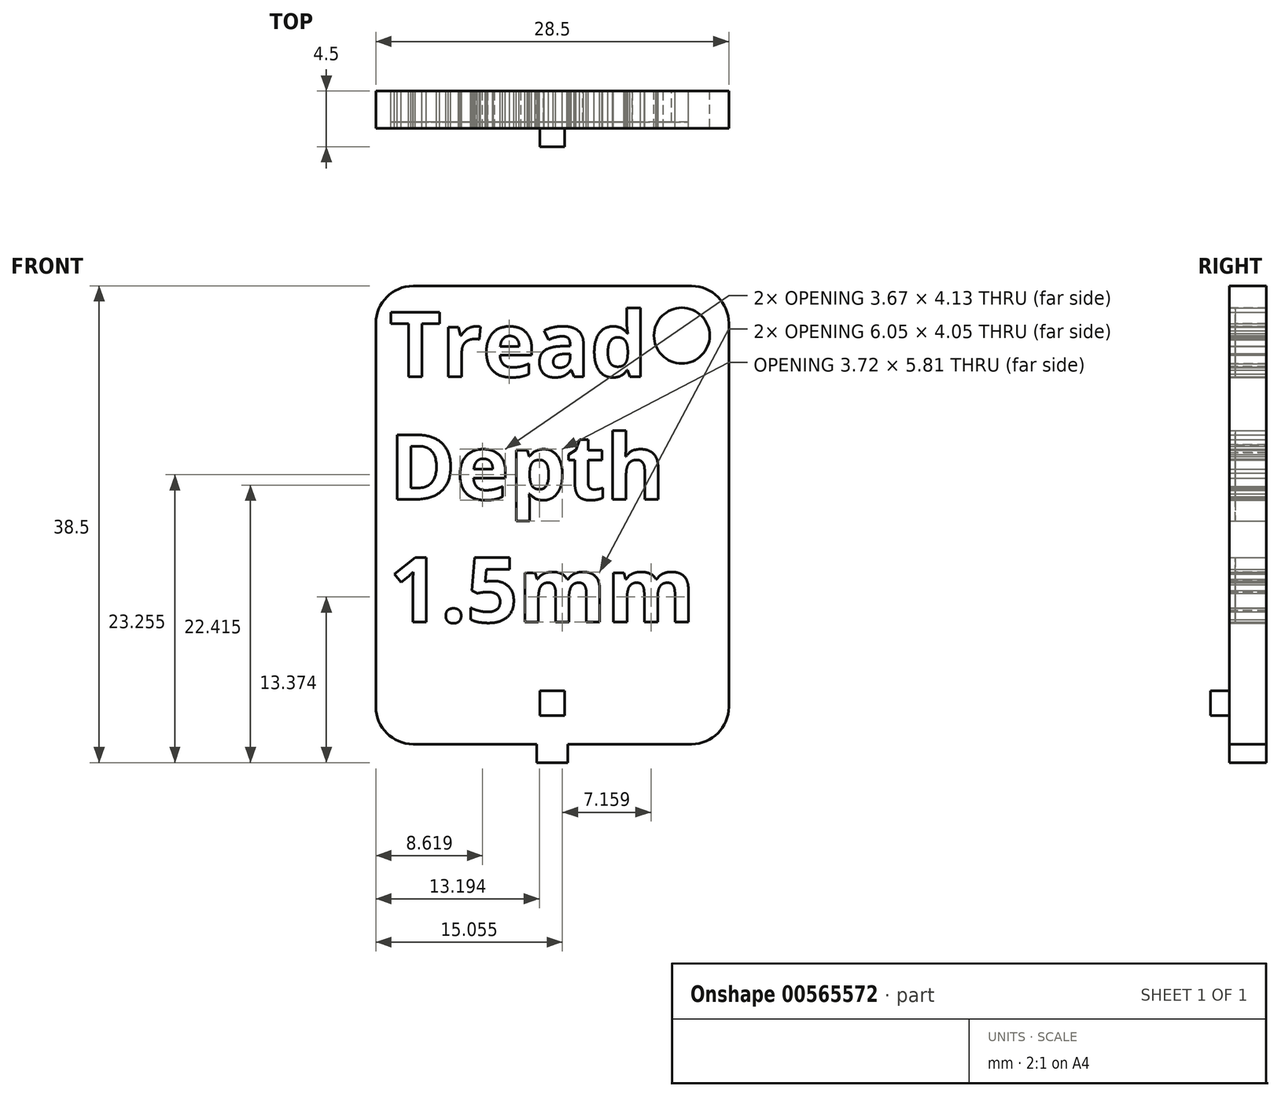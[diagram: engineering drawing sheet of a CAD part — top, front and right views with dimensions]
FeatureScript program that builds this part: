
annotation { "Feature Type Name" : "Feature", "Feature Type Description" : "" }
export const myFeature = defineFeature(function(context is Context, id is Id, definition is map)
    precondition{}
    {
        {
            var Q0;
            Q0=qCreatedBy(makeId("Front.planeOp"),FACE);
            var sketch = newSketch(context, id + "F0", { "sketchPlane" : qUnion([Q0])});
            skLineSegment(sketch, "E0.bottom", {"start": v(-50.87, 72.36) * mm, "end": v(-22.37, 72.36) * mm});
            skLineSegment(sketch, "E0.top", {"start": v(-50.87, 35.36) * mm, "end": v(-37.87, 35.36) * mm});
            skLineSegment(sketch, "E0.left", {"start": v(-50.87, 72.36) * mm, "end": v(-50.87, 35.36) * mm});
            skLineSegment(sketch, "E0.right", {"start": v(-22.37, 72.36) * mm, "end": v(-22.37, 35.36) * mm});
            skLineSegment(sketch, "E1.top", {"start": v(-37.87, 33.86) * mm, "end": v(-35.37, 33.86) * mm});
            skLineSegment(sketch, "E1.left", {"start": v(-37.87, 35.36) * mm, "end": v(-37.87, 33.86) * mm});
            skLineSegment(sketch, "E1.right", {"start": v(-35.37, 35.36) * mm, "end": v(-35.37, 33.86) * mm});
            skLineSegment(sketch, "E2.trimOffspring", {"start": v(-35.37, 35.36) * mm, "end": v(-22.37, 35.36) * mm});
            skLineSegment(sketch, "E3.bottom", {"start": v(-37.62, 37.67) * mm, "end": v(-35.62, 37.67) * mm});
            skLineSegment(sketch, "E3.top", {"start": v(-37.62, 39.67) * mm, "end": v(-35.62, 39.67) * mm});
            skLineSegment(sketch, "E3.left", {"start": v(-37.62, 37.67) * mm, "end": v(-37.62, 39.67) * mm});
            skLineSegment(sketch, "E3.right", {"start": v(-35.62, 37.67) * mm, "end": v(-35.62, 39.67) * mm});
            skText(sketch, "E4", { "text": "Tread \nDepth \n1.5mm", "fontName": "OpenSans-Bold.ttf"});
            skCircle(sketch, "E5", {"center": v(-26.16, 68.35) * mm, "radius": 2.25 * mm});
            const initialGuessF0  = {"E4": [-0.04981, 0.06504, 1, 0, 0.00525]};
            skSetInitialGuess(sketch, initialGuessF0);
            skSolve(sketch);
        }
        {
            var Q0;
            Q0=makeQuery(id+"F0.imprint","IMPRINT",FACE,{"disambiguationData":[TD([[makeQuery(id+"F0.imprint","IMPRINT",EDGE,{"derivedFrom":sQuery(id+"F0.wireOp",EDGE,"E0.bottom")}),-1.0]])]});
            var Q1;
            Q1=makeQuery(id+"F0.imprint","IMPRINT",FACE,{"disambiguationData":[TD([[makeQuery(id+"F0.imprint","IMPRINT",EDGE,{"derivedFrom":sQuery(id+"F0.wireOp",EDGE,"E4.sketch_text.stroke-65")}),1.0]])]});
            var Q2;
            Q2=makeQuery(id+"F0.imprint","IMPRINT",FACE,{"disambiguationData":[TD([[makeQuery(id+"F0.imprint","IMPRINT",EDGE,{"derivedFrom":sQuery(id+"F0.wireOp",EDGE,"E4.sketch_text.stroke-105")}),1.0]])]});
            var Q3;
            Q3=makeQuery(id+"F0.imprint","IMPRINT",FACE,{"disambiguationData":[TD([[makeQuery(id+"F0.imprint","IMPRINT",EDGE,{"derivedFrom":sQuery(id+"F0.wireOp",EDGE,"E4.sketch_text.stroke-38")}),1.0]])]});
            var Q4;
            Q4=makeQuery(id+"F0.imprint","IMPRINT",FACE,{"disambiguationData":[TD([[makeQuery(id+"F0.imprint","IMPRINT",EDGE,{"derivedFrom":sQuery(id+"F0.wireOp",EDGE,"E4.sketch_text.stroke-70")}),1.0]])]});
            var Q5;
            Q5=makeQuery(id+"F0.imprint","IMPRINT",FACE,{"disambiguationData":[TD([[makeQuery(id+"F0.imprint","IMPRINT",EDGE,{"derivedFrom":sQuery(id+"F0.wireOp",EDGE,"E4.sketch_text.stroke-96")}),1.0]])]});
            var Q6;
            Q6=makeQuery(id+"F0.imprint","IMPRINT",FACE,{"disambiguationData":[TD([[makeQuery(id+"F0.imprint","IMPRINT",EDGE,{"derivedFrom":sQuery(id+"F0.wireOp",EDGE,"E4.sketch_text.stroke-136")}),1.0]])]});
            var Q7;
            Q7=makeQuery(id+"F0.imprint","IMPRINT",FACE,{"disambiguationData":[TD([[makeQuery(id+"F0.imprint","IMPRINT",EDGE,{"derivedFrom":sQuery(id+"F0.wireOp",EDGE,"E4.sketch_text.stroke-80")}),1.0]])]});
            var Q8;
            Q8=makeQuery(id+"F0.imprint","IMPRINT",FACE,{"disambiguationData":[TD([[makeQuery(id+"F0.imprint","IMPRINT",EDGE,{"derivedFrom":sQuery(id+"F0.wireOp",EDGE,"E4.sketch_text.stroke-21")}),1.0]])]});
            extrude(context, id + "F1", {"entities" : qUnion([Q0, Q1, Q2, Q3, Q4, Q5, Q6, Q7, Q8]), "depth" : 3 * mm, "offsetDistance" : 25 * mm});
        }
        {
            var Q0;
            Q0=makeQuery(id+"F0.imprint","IMPRINT",FACE,{"disambiguationData":[TD([[makeQuery(id+"F0.imprint","IMPRINT",EDGE,{"derivedFrom":sQuery(id+"F0.wireOp",EDGE,"E4.sketch_text.stroke-0")}),-1.0]])]});
            var Q1;
            Q1=makeQuery(id+"F0.imprint","IMPRINT",FACE,{"disambiguationData":[TD([[makeQuery(id+"F0.imprint","IMPRINT",EDGE,{"derivedFrom":sQuery(id+"F0.wireOp",EDGE,"E4.sketch_text.stroke-8")}),-1.0]])]});
            var Q2;
            Q2=makeQuery(id+"F0.imprint","IMPRINT",FACE,{"disambiguationData":[TD([[makeQuery(id+"F0.imprint","IMPRINT",EDGE,{"derivedFrom":sQuery(id+"F0.wireOp",EDGE,"E4.sketch_text.stroke-25")}),-1.0]])]});
            var Q3;
            Q3=makeQuery(id+"F0.imprint","IMPRINT",FACE,{"disambiguationData":[TD([[makeQuery(id+"F0.imprint","IMPRINT",EDGE,{"derivedFrom":sQuery(id+"F0.wireOp",EDGE,"E4.sketch_text.stroke-38")}),-1.0]])]});
            var Q4;
            Q4=makeQuery(id+"F0.imprint","IMPRINT",FACE,{"disambiguationData":[TD([[makeQuery(id+"F0.imprint","IMPRINT",EDGE,{"derivedFrom":sQuery(id+"F0.wireOp",EDGE,"E4.sketch_text.stroke-58")}),-1.0]])]});
            var Q5;
            Q5=makeQuery(id+"F0.imprint","IMPRINT",FACE,{"disambiguationData":[TD([[makeQuery(id+"F0.imprint","IMPRINT",EDGE,{"derivedFrom":sQuery(id+"F0.wireOp",EDGE,"E4.sketch_text.stroke-70")}),-1.0]])]});
            var Q6;
            Q6=makeQuery(id+"F0.imprint","IMPRINT",FACE,{"disambiguationData":[TD([[makeQuery(id+"F0.imprint","IMPRINT",EDGE,{"derivedFrom":sQuery(id+"F0.wireOp",EDGE,"E4.sketch_text.stroke-90")}),-1.0]])]});
            var Q7;
            Q7=makeQuery(id+"F0.imprint","IMPRINT",FACE,{"disambiguationData":[TD([[makeQuery(id+"F0.imprint","IMPRINT",EDGE,{"derivedFrom":sQuery(id+"F0.wireOp",EDGE,"E4.sketch_text.stroke-113")}),-1.0]])]});
            var Q8;
            Q8=makeQuery(id+"F0.imprint","IMPRINT",FACE,{"disambiguationData":[TD([[makeQuery(id+"F0.imprint","IMPRINT",EDGE,{"derivedFrom":sQuery(id+"F0.wireOp",EDGE,"E4.sketch_text.stroke-131")}),-1.0]])]});
            var Q9;
            Q9=makeQuery(id+"F0.imprint","IMPRINT",FACE,{"disambiguationData":[TD([[makeQuery(id+"F0.imprint","IMPRINT",EDGE,{"derivedFrom":sQuery(id+"F0.wireOp",EDGE,"E4.sketch_text.stroke-148")}),-1.0]])]});
            var Q10;
            Q10=makeQuery(id+"F0.imprint","IMPRINT",FACE,{"disambiguationData":[TD([[makeQuery(id+"F0.imprint","IMPRINT",EDGE,{"derivedFrom":sQuery(id+"F0.wireOp",EDGE,"E4.sketch_text.stroke-158")}),-1.0]])]});
            var Q11;
            Q11=makeQuery(id+"F0.imprint","IMPRINT",FACE,{"disambiguationData":[TD([[makeQuery(id+"F0.imprint","IMPRINT",EDGE,{"derivedFrom":sQuery(id+"F0.wireOp",EDGE,"E4.sketch_text.stroke-166")}),-1.0]])]});
            var Q12;
            Q12=makeQuery(id+"F0.imprint","IMPRINT",FACE,{"disambiguationData":[TD([[makeQuery(id+"F0.imprint","IMPRINT",EDGE,{"derivedFrom":sQuery(id+"F0.wireOp",EDGE,"E4.sketch_text.stroke-186")}),-1.0]])]});
            var Q13;
            Q13=makeQuery(id+"F0.imprint","IMPRINT",FACE,{"disambiguationData":[TD([[makeQuery(id+"F0.imprint","IMPRINT",EDGE,{"derivedFrom":sQuery(id+"F0.wireOp",EDGE,"E4.sketch_text.stroke-214")}),-1.0]])]});
            var Q14;
            Q14=makeQuery(id+"F0.imprint","IMPRINT",FACE,{"disambiguationData":[TD([[makeQuery(id+"F0.imprint","IMPRINT",EDGE,{"derivedFrom":sQuery(id+"F0.wireOp",EDGE,"E4.sketch_text.stroke-217")}),-1.0]])]});
            var Q15;
            Q15=makeQuery(id+"F0.imprint","IMPRINT",FACE,{"disambiguationData":[TD([[makeQuery(id+"F0.imprint","IMPRINT",EDGE,{"derivedFrom":sQuery(id+"F0.wireOp",EDGE,"E4.sketch_text.stroke-245")}),-1.0]])]});
            var Q16;
            Q16=makeQuery(id+"F0.imprint","IMPRINT",FACE,{"disambiguationData":[TD([[makeQuery(id+"F0.imprint","IMPRINT",EDGE,{"derivedFrom":sQuery(id+"F0.wireOp",EDGE,"E4.sketch_text.stroke-189")}),-1.0]])]});
            extrude(context, id + "F2", {"entities" : qUnion([Q0, Q1, Q2, Q3, Q4, Q5, Q6, Q7, Q8, Q9, Q10, Q11, Q12, Q13, Q14, Q15, Q16]), "depth" : 2.5 * mm, "offsetDistance" : 25 * mm});
        }
        {
            var Q0;
            Q0=makeQuery(id+"F0.imprint","IMPRINT",FACE,{"disambiguationData":[TD([[makeQuery(id+"F0.imprint","IMPRINT",EDGE,{"derivedFrom":sQuery(id+"F0.wireOp",EDGE,"E3.bottom")}),1.0]])]});
            extrude(context, id + "F3", {"entities" : qUnion([Q0]), "operationType" : NewBodyOperationType.ADD, "depth" : 4.5 * mm, "offsetDistance" : 25 * mm});
        }
        {
            var Q0;
            Q0=makeQuery(id+"F1.opExtrude","SWEPT_EDGE",EDGE,{"disambiguationData":[OSD([sQuery(id+"F0.wireOp",EDGE,"E0.right"),sQuery(id+"F0.wireOp",EDGE,"E2.trimOffspring")])]});
            var Q1;
            Q1=makeQuery(id+"F1.opExtrude","SWEPT_EDGE",EDGE,{"disambiguationData":[OSD([sQuery(id+"F0.wireOp",EDGE,"E0.bottom"),sQuery(id+"F0.wireOp",EDGE,"E0.right")])]});
            var Q2;
            Q2=makeQuery(id+"F1.opExtrude","SWEPT_EDGE",EDGE,{"disambiguationData":[OSD([sQuery(id+"F0.wireOp",EDGE,"E0.top"),sQuery(id+"F0.wireOp",EDGE,"E0.left")])]});
            var Q3;
            Q3=makeQuery(id+"F1.opExtrude","SWEPT_EDGE",EDGE,{"disambiguationData":[OSD([sQuery(id+"F0.wireOp",EDGE,"E0.bottom"),sQuery(id+"F0.wireOp",EDGE,"E0.left")])]});
            fillet(context, id + "F4", {"entities" : qUnion([Q0, Q1, Q2, Q3]), "radius" : 3 * mm, "tangentPropagation" : true, "allowEdgeOverflow" : false});
        }
    });
